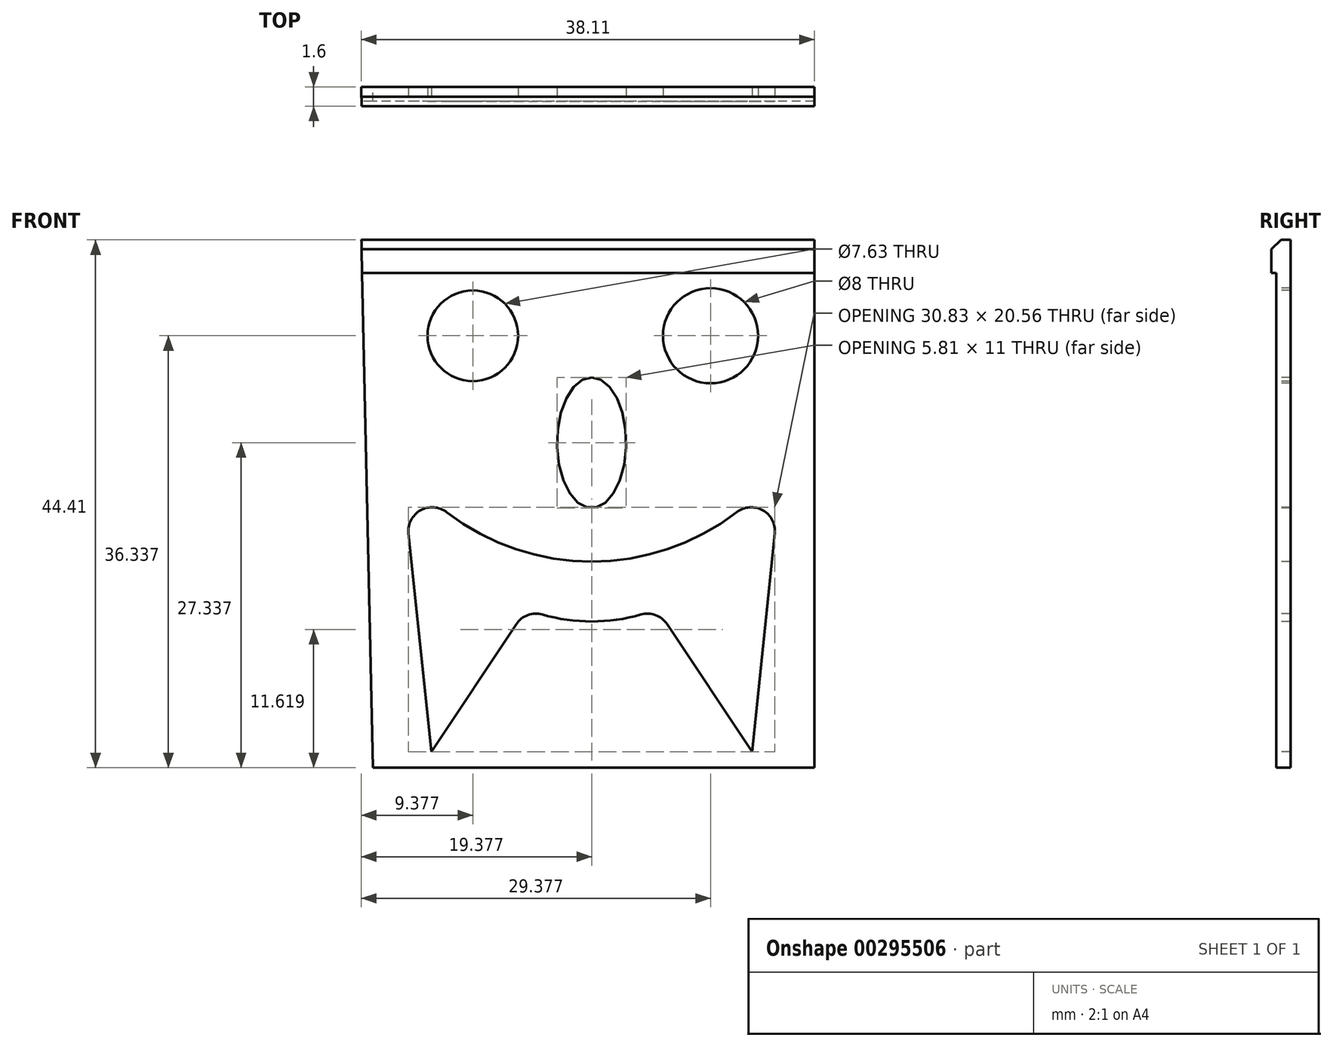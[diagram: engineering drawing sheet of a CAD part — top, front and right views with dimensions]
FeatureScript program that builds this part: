
annotation { "Feature Type Name" : "Feature", "Feature Type Description" : "" }
export const myFeature = defineFeature(function(context is Context, id is Id, definition is map)
    precondition{}
    {
        {
            var Q0;
            Q0=qCreatedBy(makeId("Front.planeOp"),FACE);
            var sketch = newSketch(context, id + "F0", { "sketchPlane" : qUnion([Q0])});
            skLineSegment(sketch, "E0.bottom", {"start": v(-65, 60) * mm, "end": v(65, 60) * mm});
            skLineSegment(sketch, "E0.top", {"start": v(-65, -20) * mm, "end": v(65, -20) * mm});
            skLineSegment(sketch, "E0.left", {"start": v(-65, 60) * mm, "end": v(-65, -20) * mm});
            skLineSegment(sketch, "E0.right", {"start": v(65, 60) * mm, "end": v(65, -20) * mm});
            skSolve(sketch);
        }
        {
            var Q0;
            Q0=qSketchRegion(id+"F0",true);
            extrude(context, id + "F1", {"entities" : qUnion([Q0]), "depth" : 1.6 * mm});
        }
        {
            var Q0;
            Q0=makeQuery(id+"F1.opExtrude","CAP_FACE",FACE,{"disambiguationData":[OSD([sQuery(id+"F0.wireOp",EDGE,"E0.bottom"),sQuery(id+"F0.wireOp",EDGE,"E0.top"),sQuery(id+"F0.wireOp",EDGE,"E0.left"),sQuery(id+"F0.wireOp",EDGE,"E0.right")])],"isStart":false});
            var sketch = newSketch(context, id + "F2", { "sketchPlane" : qUnion([Q0])});
            skText(sketch, "E1", { "text": "VLAD", "fontName": "AllertaStencil-Regular.ttf"});
            skText(sketch, "E2", { "text": "♥", "fontName": "NotoSansCJKjp-Regular.otf"});
            const initialGuessF2  = {"E1": [-0.055, -0.01313, 1, 0, 0.0285], "E2": [0.0007, 0.01874, 1, 0, 0.032]};
            skSetInitialGuess(sketch, initialGuessF2);
            skSolve(sketch);
        }
        {
            var Q0;
            Q0=qSketchRegion(id+"F2",true);
            extrude(context, id + "F3", {"entities" : qUnion([Q0]), "operationType" : NewBodyOperationType.REMOVE, "endBound" : BoundingType.THROUGH_ALL, "oppositeDirection" : true, "depth" : 25 * mm});
        }
        {
            var Q0;
            Q0=makeQuery(id+"F1.opExtrude","SWEPT_EDGE",EDGE,{"disambiguationData":[OSD([sQuery(id+"F0.wireOp",EDGE,"E0.top"),sQuery(id+"F0.wireOp",EDGE,"E0.right")])]});
            var Q1;
            Q1=makeQuery(id+"F1.opExtrude","SWEPT_EDGE",EDGE,{"disambiguationData":[OSD([sQuery(id+"F0.wireOp",EDGE,"E0.bottom"),sQuery(id+"F0.wireOp",EDGE,"E0.right")])]});
            var Q2;
            Q2=makeQuery(id+"F1.opExtrude","SWEPT_EDGE",EDGE,{"disambiguationData":[OSD([sQuery(id+"F0.wireOp",EDGE,"E0.top"),sQuery(id+"F0.wireOp",EDGE,"E0.left")])]});
            var Q3;
            Q3=makeQuery(id+"F1.opExtrude","SWEPT_EDGE",EDGE,{"disambiguationData":[OSD([sQuery(id+"F0.wireOp",EDGE,"E0.bottom"),sQuery(id+"F0.wireOp",EDGE,"E0.left")])]});
            fillet(context, id + "F4", {"entities" : qUnion([Q0, Q1, Q2, Q3]), "radius" : 20 * mm, "tangentPropagation" : true, "allowEdgeOverflow" : false});
        }
        {
            var Q0;
            Q0=makeQuery(id+"F1.opExtrude","CAP_EDGE",EDGE,{"disambiguationData":[OSD([sQuery(id+"F0.wireOp",EDGE,"E0.top")])],"isStart":false});
            chamfer(context, id + "F5", {"entities" : qUnion([Q0]), "width" : 0.8 * mm, "tangentPropagation" : true});
        }
        {
            var Q0;
            Q0=makeQuery(id+"F1.opExtrude","CAP_FACE",FACE,{"disambiguationData":[OSD([sQuery(id+"F0.wireOp",EDGE,"E0.bottom"),sQuery(id+"F0.wireOp",EDGE,"E0.top"),sQuery(id+"F0.wireOp",EDGE,"E0.left"),sQuery(id+"F0.wireOp",EDGE,"E0.right")])],"isStart":false});
            var sketch = newSketch(context, id + "F6", { "sketchPlane" : qUnion([Q0])});
            skCircle(sketch, "E3", {"center": v(-35.7, 51.93) * mm, "radius": 3.82 * mm});
            skCircle(sketch, "E4", {"center": v(-15.7, 51.93) * mm, "radius": 4 * mm});
            skEllipse(sketch, "E5", {"center": v(-25.7, 42.93) * mm, "majorRadius": 5.5 * mm, "minorRadius": 2.9 * mm, "majorAxis": v(0, 1)});
            skArc(sketch, "E6", {"start": v(-41.7, 40.93) * mm, "mid": v(-25.7, 32.93) * mm, "end": v(-9.7, 40.93) * mm});
            skLineSegment(sketch, "E7", {"start": v(-41.7, 40.93) * mm, "end": v(-39.2, 16.93) * mm});
            skLineSegment(sketch, "E8", {"start": v(-39.2, 16.93) * mm, "end": v(-31.2, 28.93) * mm});
            skLineSegment(sketch, "E9", {"start": v(-25.7, 42.93) * mm, "end": v(-25.7, 20.3) * mm, "construction": true});
            skLineSegment(sketch, "E10", {"start": v(-9.7, 40.93) * mm, "end": v(-12.2, 16.93) * mm});
            skLineSegment(sketch, "E11", {"start": v(-12.2, 16.93) * mm, "end": v(-20.2, 28.93) * mm});
            skArc(sketch, "E12", {"start": v(-31.2, 28.93) * mm, "mid": v(-25.7, 27.89) * mm, "end": v(-20.2, 28.93) * mm});
            skSolve(sketch);
        }
        {
            var Q0;
            Q0=qSketchRegion(id+"F6",true);
            extrude(context, id + "F7", {"entities" : qUnion([Q0]), "operationType" : NewBodyOperationType.REMOVE, "endBound" : BoundingType.THROUGH_ALL, "oppositeDirection" : true, "depth" : 25 * mm});
        }
        {
            var Q0;
            Q0=makeQuery(id+"F1.opExtrude","CAP_FACE",FACE,{"disambiguationData":[OSD([sQuery(id+"F0.wireOp",EDGE,"E0.bottom"),sQuery(id+"F0.wireOp",EDGE,"E0.top"),sQuery(id+"F0.wireOp",EDGE,"E0.left"),sQuery(id+"F0.wireOp",EDGE,"E0.right")])],"isStart":false});
            var sketch = newSketch(context, id + "F8", { "sketchPlane" : qUnion([Q0])});
            skLineSegment(sketch, "E13.0", {"start": v(-45, -17.2) * mm, "end": v(45, -17.2) * mm});
            skArc(sketch, "E13.1", {"start": v(-62.2, 0) * mm, "mid": v(-57.16, -12.16) * mm, "end": v(-45, -17.2) * mm});
            skArc(sketch, "E13.2", {"start": v(45, -17.2) * mm, "mid": v(57.16, -12.16) * mm, "end": v(62.2, 0) * mm});
            skLineSegment(sketch, "E13.3", {"start": v(-62.2, 40) * mm, "end": v(-62.2, 0) * mm});
            skLineSegment(sketch, "E13.4", {"start": v(62.2, 0) * mm, "end": v(62.2, 40) * mm});
            skArc(sketch, "E13.5", {"start": v(62.2, 40) * mm, "mid": v(57.16, 52.16) * mm, "end": v(45, 57.2) * mm});
            skLineSegment(sketch, "E13.6", {"start": v(45, 57.2) * mm, "end": v(-45, 57.2) * mm});
            skArc(sketch, "E13.7", {"start": v(-45, 57.2) * mm, "mid": v(-57.16, 52.16) * mm, "end": v(-62.2, 40) * mm});
            skSolve(sketch);
        }
        {
            var Q0;
            Q0=qSketchRegion(id+"F8",true);
            extrude(context, id + "F9", {"entities" : qUnion([Q0]), "operationType" : NewBodyOperationType.REMOVE, "oppositeDirection" : true, "depth" : 0.4 * mm});
        }
        {
            var Q0;
            Q0=makeQuery(id+"F9.boolean.opBoolean","COPY",FACE,{"derivedFrom":makeQuery(id+"F9.opExtrude","CAP_FACE",FACE,{"disambiguationData":[OSD([sQuery(id+"F8.wireOp",EDGE,"E13.0"),sQuery(id+"F8.wireOp",EDGE,"E13.1"),sQuery(id+"F8.wireOp",EDGE,"E13.2"),sQuery(id+"F8.wireOp",EDGE,"E13.3"),sQuery(id+"F8.wireOp",EDGE,"E13.4"),sQuery(id+"F8.wireOp",EDGE,"E13.5"),sQuery(id+"F8.wireOp",EDGE,"E13.6"),sQuery(id+"F8.wireOp",EDGE,"E13.7")])],"isStart":false})});
            var sketch = newSketch(context, id + "F10", { "sketchPlane" : qUnion([Q0])});
            skLineSegment(sketch, "E14", {"start": v(28.92, 53.56) * mm, "end": v(22.93, 51.5) * mm});
            skLineSegment(sketch, "E15", {"start": v(22.93, 51.5) * mm, "end": v(16.92, 53.57) * mm});
            skLineSegment(sketch, "E16", {"start": v(16.92, 53.57) * mm, "end": v(16.92, 45.28) * mm});
            skLineSegment(sketch, "E17", {"start": v(16.92, 45.28) * mm, "end": v(29.17, 45.28) * mm});
            skLineSegment(sketch, "E18", {"start": v(29.17, 45.28) * mm, "end": v(28.92, 53.56) * mm});
            skSolve(sketch);
        }
        {
            var Q0;
            Q0=qSketchRegion(id+"F10",true);
            extrude(context, id + "F11", {"entities" : qUnion([Q0]), "operationType" : NewBodyOperationType.REMOVE, "oppositeDirection" : true, "depth" : 25 * mm});
        }
        {
            var Q0;
            Q0=makeQuery(id+"F7.boolean.opBoolean","COPY",EDGE,{"derivedFrom":makeQuery(id+"F7.opExtrude","SWEPT_EDGE",EDGE,{"disambiguationData":[OSD([sQuery(id+"F6.wireOp",EDGE,"E6"),sQuery(id+"F6.wireOp",EDGE,"E10")])]})});
            var Q1;
            Q1=makeQuery(id+"F7.boolean.opBoolean","COPY",EDGE,{"derivedFrom":makeQuery(id+"F7.opExtrude","SWEPT_EDGE",EDGE,{"disambiguationData":[OSD([sQuery(id+"F6.wireOp",EDGE,"E6"),sQuery(id+"F6.wireOp",EDGE,"E7")])]})});
            var Q2;
            Q2=makeQuery(id+"F7.boolean.opBoolean","COPY",EDGE,{"derivedFrom":makeQuery(id+"F7.opExtrude","SWEPT_EDGE",EDGE,{"disambiguationData":[OSD([sQuery(id+"F6.wireOp",EDGE,"E11"),sQuery(id+"F6.wireOp",EDGE,"E12")])]})});
            var Q3;
            Q3=makeQuery(id+"F7.boolean.opBoolean","COPY",EDGE,{"derivedFrom":makeQuery(id+"F7.opExtrude","SWEPT_EDGE",EDGE,{"disambiguationData":[OSD([sQuery(id+"F6.wireOp",EDGE,"E8"),sQuery(id+"F6.wireOp",EDGE,"E12")])]})});
            fillet(context, id + "F12", {"entities" : qUnion([Q0, Q1, Q2, Q3]), "radius" : 2 * mm, "tangentPropagation" : true, "allowEdgeOverflow" : false});
        }
        {
            var Q0;
            Q0=qCreatedBy(makeId("Front.planeOp"),FACE);
            var sketch = newSketch(context, id + "F13", { "sketchPlane" : qUnion([Q0])});
            skLineSegment(sketch, "E19.top", {"start": v(-44.12, 15.6) * mm, "end": v(-6.97, 15.6) * mm});
            skLineSegment(sketch, "E20", {"start": v(-6.97, 15.6) * mm, "end": v(-6.97, 66.21) * mm});
            skLineSegment(sketch, "E21", {"start": v(-6.97, 66.21) * mm, "end": v(67.15, 66.21) * mm});
            skLineSegment(sketch, "E22", {"start": v(67.15, 66.21) * mm, "end": v(67.15, -27.66) * mm});
            skLineSegment(sketch, "E23", {"start": v(67.15, -27.66) * mm, "end": v(-72.95, -27.66) * mm});
            skLineSegment(sketch, "E24", {"start": v(-72.95, -27.66) * mm, "end": v(-72.95, 66.21) * mm});
            skLineSegment(sketch, "E25", {"start": v(-72.95, 66.21) * mm, "end": v(-45.21, 66.21) * mm});
            skLineSegment(sketch, "E26", {"start": v(-45.21, 66.21) * mm, "end": v(-44.12, 15.6) * mm});
            skSolve(sketch);
        }
        {
            var Q0;
            Q0 = qSketchRegion(id + "F13", true);
            extrude(context, id + "F14", {"entities" : qUnion([Q0]), "operationType" : NewBodyOperationType.REMOVE, "depth" : 25 * mm});
        }
    });
